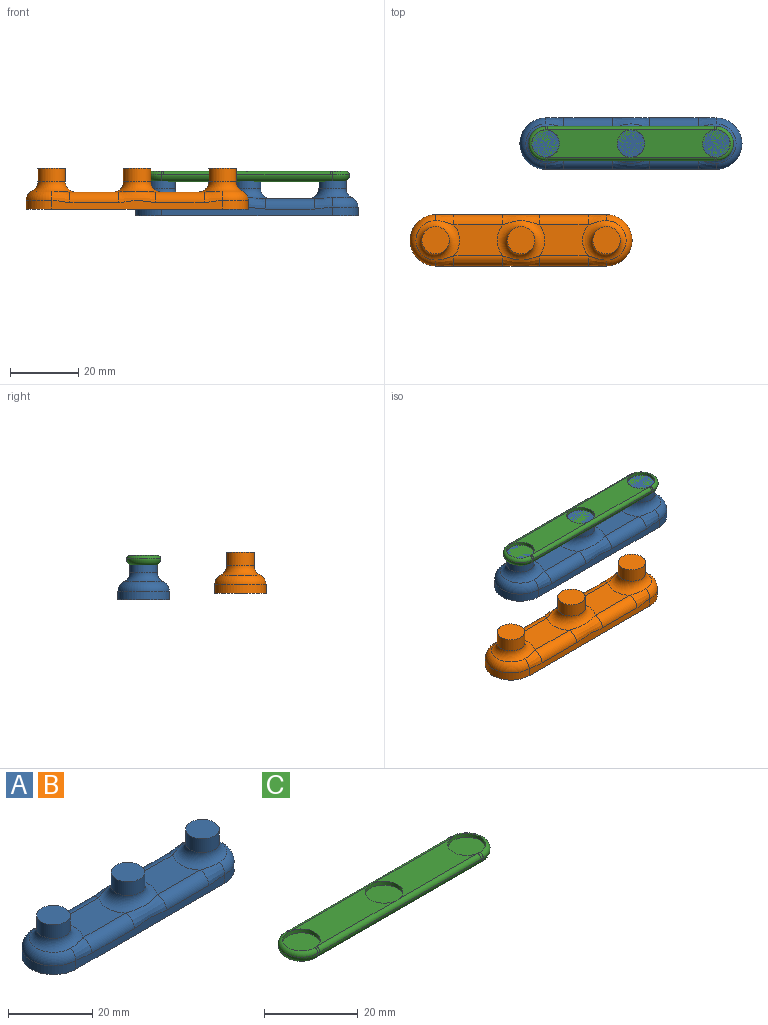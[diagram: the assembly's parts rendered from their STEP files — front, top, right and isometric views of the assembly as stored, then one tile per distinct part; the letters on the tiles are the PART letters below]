
ASSEMBLY  parts=3 mates=1
PART A: 28 faces, bbox 69.8x19.8x12 mm
  f0: plane 14.28x9mm, normal (0,0,1), area 108.3mm2, adj f9,f12,f23,f24
  f1: cylinder r=7.5mm len=15mm, axis (0,0,-1), area 60mm2, adj f2,f4,f6,f16
  f2: plane 50x2.55mm, normal (0,-1,0), area 105.8mm2, adj f1,f3,f6,f17,f19,f21,f23,f25
  f3: cylinder r=7.5mm len=15mm, axis (0,0,-1), area 60mm2, adj f2,f4,f6,f27
  f4: plane 50x2.55mm, normal (0,1,0), area 105.8mm2, adj f1,f3,f6,f18,f20,f22,f24,f26
  f5: plane 14.28x9mm, normal (0,0,1), area 108.3mm2, adj f9,f15,f19,f20
  f6: plane 65x15mm, normal (0,0,-1), area 926.7mm2, adj f1,f2,f3,f4
  f7: cylinder r=4mm len=8mm, axis (0,0,-1), area 100.5mm2, adj f8,f9
  f8: plane 8x8mm, normal (0,0,1), area 50.3mm2, adj f7
  f9: torus R=7mm, axis (0,0,1), area 130mm2, adj f0,f5,f7,f21,f22
  f10: cylinder r=4mm len=8mm, axis (0,0,-1), area 100.5mm2, adj f11,f12
  f11: plane 8x8mm, normal (0,0,1), area 50.3mm2, adj f10
  f12: torus R=7mm, axis (0,0,1), area 114.6mm2, adj f0,f10,f25,f26,f27
  f13: cylinder r=4mm len=8mm, axis (0,0,-1), area 100.5mm2, adj f14,f15
  f14: plane 8x8mm, normal (0,0,1), area 50.3mm2, adj f13
  f15: torus R=7mm, axis (0,0,1), area 114.6mm2, adj f5,f13,f16,f17,f18
  f16: torus R=4.5mm, axis (0,0,-1), area 74.1mm2, adj f1,f15,f17,f18
  f17: bspline ~8.61x3.55mm, area 21.1mm2, adj f2,f15,f16,f19
  f18: bspline ~6.66x3.27mm, area 21.1mm2, adj f4,f15,f16,f20
  f19: cylinder r=3mm len=14.28mm, axis (-1,0,0), area 67.3mm2, adj f2,f5,f17,f21
  f20: cylinder r=3mm len=14.28mm, axis (1,0,0), area 67.3mm2, adj f4,f5,f18,f22
  f21: bspline ~12.97x3.55mm, area 42.1mm2, adj f2,f9,f19,f23
  f22: bspline ~12.97x3.55mm, area 42.1mm2, adj f4,f9,f20,f24
  f23: cylinder r=3mm len=14.28mm, axis (-1,0,0), area 67.3mm2, adj f0,f2,f21,f25
  f24: cylinder r=3mm len=14.28mm, axis (1,0,0), area 67.3mm2, adj f0,f4,f22,f26
  f25: bspline ~6.66x3.27mm, area 21.1mm2, adj f2,f12,f23,f27
  f26: bspline ~8.61x3.55mm, area 21.1mm2, adj f4,f12,f24,f27
  f27: torus R=4.5mm, axis (0,0,-1), area 74.1mm2, adj f3,f12,f25,f26
PART B: same geometry as A
PART C: 27 faces, bbox 60.8x10.8x3.4 mm
  f0: plane 0.63x0mm, normal (0,-1,0), area 0mm2, adj f3,f16,f23
  f1: plane 0.63x0mm, normal (0,1,0), area 0mm2, adj f5,f21,f26
  f2: plane 23.73x8mm, normal (0,0,1), area 148.6mm2, adj f9,f13,f18,f19
  f3: cylinder r=5mm len=10mm, axis (0,0,1), area 0mm2, adj f0,f6,f15,f25
  f4: plane 0.63x0mm, normal (0,-1,0), area 0mm2, adj f5,f20,f23
  f5: cylinder r=5mm len=10mm, axis (0,0,1), area 0mm2, adj f1,f4,f22,f24
  f6: plane 0.63x0mm, normal (0,1,0), area 0mm2, adj f3,f17,f26
  f7: plane 56x6mm, normal (0,0,-1), area 328.3mm2, adj f23,f24,f25,f26
  f8: plane 23.73x8mm, normal (0,0,1), area 148.6mm2, adj f9,f11,f18,f19
  f9: cylinder r=4.05mm len=8.1mm, axis (0,0,1), area 25.4mm2, adj f2,f8,f10,f18,f19
  f10: plane 8.1x8.1mm, normal (0,0,1), area 51.5mm2, adj f9
  f11: cylinder r=4.05mm len=8.1mm, axis (0,0,1), area 25.4mm2, adj f8,f12,f15,f16,f17
  f12: plane 8.1x8.1mm, normal (0,0,1), area 51.5mm2, adj f11
  f13: cylinder r=4.05mm len=8.1mm, axis (0,0,1), area 25.4mm2, adj f2,f14,f20,f21,f22
  f14: plane 8.1x8.1mm, normal (0,0,1), area 51.5mm2, adj f13
  f15: torus R=4mm, axis (0,0,1), area 22.2mm2, adj f3,f11,f16,f17
  f16: bspline ~1.15x1.08mm, area 1mm2, adj f0,f11,f15,f18
  f17: bspline ~1.15x1.08mm, area 1mm2, adj f6,f11,f15,f19
  f18: cylinder r=1mm len=48.73mm, axis (1,0,0), area 76.5mm2, adj f2,f8,f9,f16,f20,f23
  f19: cylinder r=1mm len=48.73mm, axis (-1,0,0), area 76.5mm2, adj f2,f8,f9,f17,f21,f26
  f20: bspline ~1.15x1.08mm, area 1mm2, adj f4,f13,f18,f22
  f21: bspline ~1.15x1.08mm, area 1mm2, adj f1,f13,f19,f22
  f22: torus R=4mm, axis (0,0,1), area 22.2mm2, adj f5,f13,f20,f21
  f23: cylinder r=2mm len=50mm, axis (-1,0,0), area 157.1mm2, adj f0,f4,f7,f18,f24,f25
  f24: torus R=3mm, axis (0,0,1), area 42.2mm2, adj f5,f7,f23,f26
  f25: torus R=3mm, axis (0,0,1), area 42.2mm2, adj f3,f7,f23,f26
  f26: cylinder r=2mm len=50mm, axis (1,0,0), area 157.1mm2, adj f1,f6,f7,f19,f24,f25
PLACE A t=(10,6.24,-10.81)mm
PLACE B t=(-22.16,-22.08,-8.85)mm
PLACE C t=(10,6.24,2.19)mm
MATE fastened A.f7 <-> C.f9  axis (0,0,1) through (10,6.24,1.19)mm
